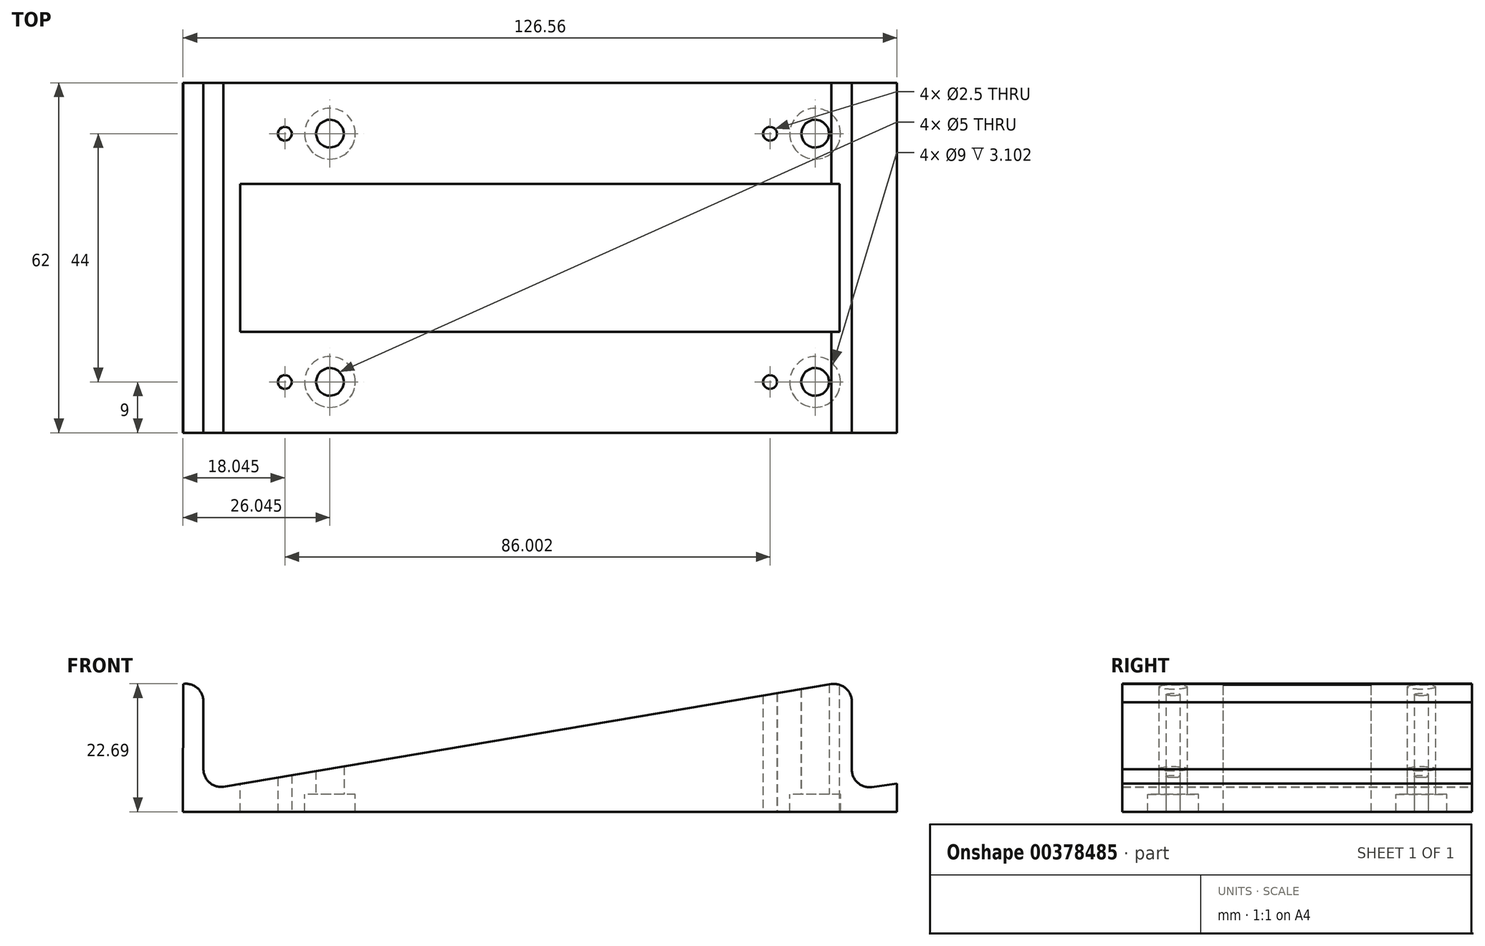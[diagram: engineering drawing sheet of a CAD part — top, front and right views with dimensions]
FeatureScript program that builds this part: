
annotation { "Feature Type Name" : "Feature", "Feature Type Description" : "" }
export const myFeature = defineFeature(function(context is Context, id is Id, definition is map)
    precondition{}
    {
        {
            var Q0;
            Q0=qCreatedBy(makeId("Front.planeOp"),FACE);
            var sketch = newSketch(context, id + "F0", { "sketchPlane" : qUnion([Q0])});
            skLineSegment(sketch, "E0", {"start": v(-59.65, 8.39) * mm, "end": v(-59.65, -3.51) * mm});
            skLineSegment(sketch, "E1", {"start": v(-56.14, -6.69) * mm, "end": v(51.65, 11.51) * mm});
            skLineSegment(sketch, "E2", {"start": v(58.81, -6.74) * mm, "end": v(63.28, -6.13) * mm});
            skLineSegment(sketch, "E3", {"start": v(63.28, -6.13) * mm, "end": v(63.28, -11.1) * mm});
            skLineSegment(sketch, "E4", {"start": v(63.28, -11.1) * mm, "end": v(-63.28, -11.1) * mm});
            skPoint(sketch, "E5.second.point", {"position": v(-62.39, -0.66) * mm});
            skPoint(sketch, "E5.third.point", {"position": v(-61.5, -0.4) * mm});
            skLineSegment(sketch, "E6", {"start": v(-63.28, -11.1) * mm, "end": v(-63.25, 11.55) * mm});
            skArc(sketch, "E7.trimOffspring", {"start": v(-59.65, 8.39) * mm, "mid": v(-60.72, 10.8) * mm, "end": v(-63.25, 11.55) * mm});
            skArc(sketch, "E8.trimOffspring", {"start": v(-59.65, -3.51) * mm, "mid": v(-58.62, -5.9) * mm, "end": v(-56.14, -6.69) * mm});
            skLineSegment(sketch, "E9", {"start": v(55.26, 8.33) * mm, "end": v(55.26, -3.56) * mm});
            skPoint(sketch, "E10.second.point", {"position": v(52.53, 5.28) * mm});
            skPoint(sketch, "E10.third.point", {"position": v(53.41, 5.54) * mm});
            skArc(sketch, "E11.trimOffspring", {"start": v(55.26, 8.33) * mm, "mid": v(54.2, 10.77) * mm, "end": v(51.65, 11.51) * mm});
            skArc(sketch, "E12.trimOffspring", {"start": v(55.26, -3.56) * mm, "mid": v(56.3, -5.97) * mm, "end": v(58.81, -6.74) * mm});
            skLineSegment(sketch, "E13", {"start": v(-63.25, 11.55) * mm, "end": v(74.42, 11.55) * mm, "construction": true});
            skSolve(sketch);
        }
        {
            var Q0;
            Q0=qSketchRegion(id+"F0",true);
            extrude(context, id + "F1", {"entities" : qUnion([Q0]), "depth" : 31 * mm});
        }
        {
            var Q0;
            Q0=makeQuery(id+"F1.opExtrude","SWEPT_BODY",BODY,{"disambiguationData":[OSD([sQuery(id+"F0.wireOp",EDGE,"X6rjagLQ-a7nE-w6Vv-3kkp-7P13FhxgeZci"),sQuery(id+"F0.wireOp",EDGE,"rJyHTlbv-r2ii-XpOz-qJYI-U7K787FcXT9B"),sQuery(id+"F0.wireOp",EDGE,"UvdABgA3-ZW4Q-jLAG-XZ58-KKb7sOvCEOLd"),sQuery(id+"F0.wireOp",EDGE,"8edDvAp8-Iqhi-MEnT-EPyK-PEICCKXdPERf"),sQuery(id+"F0.wireOp",EDGE,"5RGPJcfQ-oj1C-nyjU-RGCH-90OYZvmU7okd"),sQuery(id+"F0.wireOp",EDGE,"nuv1YldQ-uPeo-ucQy-kADE-yY51GJk1A8SW"),sQuery(id+"F0.wireOp",EDGE,"9IDJZypg-6hYg-XQDT-bXzg-yLjlFXgnIsPx"),sQuery(id+"F0.wireOp",EDGE,"5iBKq289-l9G4-ML6G-8Zm8-TBxTwmMSXo4c"),sQuery(id+"F0.wireOp",EDGE,"IRYstpvA-wG3c-Vhfm-dOiz-6G3TYm6s6ACp"),sQuery(id+"F0.wireOp",EDGE,"2tByvbzq-CgVc-BYaI-5mh9-BZhoFNA3rnU8"),sQuery(id+"F0.wireOp",EDGE,"J7kD6OiI-x1CE-zV7k-Ksf5-dgG7n0Ed7Lc8"),sQuery(id+"F0.wireOp",EDGE,"usFKVQ05-AxXf-UbQ5-ZF47-bucorxKLPDnf"),sQuery(id+"F0.wireOp",EDGE,"8tTMBYnK-jyrt-QZZi-OOM1-Ks7T1jKqHP4p"),sQuery(id+"F0.wireOp",EDGE,"aNOa8qk4-dDGC-TJfr-UsXt-0Z27L2bBaoPW"),sQuery(id+"F0.wireOp",EDGE,"co3yBv09-4AA5-sSzz-sbZm-wbczN9zzpFlO"),sQuery(id+"F0.wireOp",EDGE,"9luTmkGo-JmTk-WoZm-WdZi-2eskqThg4CA5"),sQuery(id+"F0.wireOp",EDGE,"QNMAagQt-4OmV-3ZdT-NZHn-lJ6LHsVNZ12A"),sQuery(id+"F0.wireOp",EDGE,"E0"),sQuery(id+"F0.wireOp",EDGE,"LaCQxE5r-Ou8T-tspR-dPCc-d2gM8dt26IJ4"),sQuery(id+"F0.wireOp",EDGE,"tysDmkrt-YQUX-nmhd-IIcf-EuzOKTVKjwW1"),sQuery(id+"F0.wireOp",EDGE,"8zM2XU66-CfLp-DSu5-ggFv-Xjqba4kKd3lN"),sQuery(id+"F0.wireOp",EDGE,"bxPwawIe-VsdV-0K0X-kh71-O9GE0I0d2Hzn"),sQuery(id+"F0.wireOp",EDGE,"Ta76Hruu-mcOr-gASH-Amss-OitY1s99El2f"),sQuery(id+"F0.wireOp",EDGE,"9uWYvEGJ-saeM-Nbb3-zuV6-ds3pb9swBQfK"),sQuery(id+"F0.wireOp",EDGE,"9eZR5atI-s3yS-Bz70-sCyy-oXYN0rDXefjr"),sQuery(id+"F0.wireOp",EDGE,"foBjDoMU-IZlR-ykUg-u7Yn-BJamdywYEiWy"),sQuery(id+"F0.wireOp",EDGE,"fnvSqjr0-rV7v-3WBg-xxCd-QbMLTEKwFvC4"),sQuery(id+"F0.wireOp",EDGE,"z3XylwKl-Yxo3-bV3A-yvAI-vIvSsyK3gtAu"),sQuery(id+"F0.wireOp",EDGE,"E1"),sQuery(id+"F0.wireOp",EDGE,"2c2nu2O0-qx7z-G40k-56CR-Hb7mX1kJGF1D"),sQuery(id+"F0.wireOp",EDGE,"W6u8q2Sr-tn2T-pBh1-jTxB-UCteOMF8OT5b"),sQuery(id+"F0.wireOp",EDGE,"SP8eBbsK-gR6C-g5yt-1Xhk-VaCtSweUHDhg"),sQuery(id+"F0.wireOp",EDGE,"F2eFEpuX-bTFf-0sAG-GLRY-GrkC39FuYopk"),sQuery(id+"F0.wireOp",EDGE,"B11oUoTT-6qet-d9Tf-xIA7-Onbt0dr6JRqB"),sQuery(id+"F0.wireOp",EDGE,"icmsBmHN-4xDo-8gjD-Ngl4-kt1qITF5Sr4D"),sQuery(id+"F0.wireOp",EDGE,"MzAjo3WH-x5B9-fS6W-S6Yf-auPV0ZSmn7rd"),sQuery(id+"F0.wireOp",EDGE,"3tkOM3FL-qgvZ-PLIy-XY6Q-vuf0hc8dh5GJ"),sQuery(id+"F0.wireOp",EDGE,"uJlCFYyk-phwo-ZUq8-5xq0-rSjuSznOMZrS"),sQuery(id+"F0.wireOp",EDGE,"mkuXqJka-q1Q0-TAYG-IULb-ylSPT2SN1lg7"),sQuery(id+"F0.wireOp",EDGE,"3tb4hQMN-rnYG-9bp3-TFDC-0CORyscKgtPi"),sQuery(id+"F0.wireOp",EDGE,"k8RofrE4-9yto-xs5X-iHqh-SwSJ6BzJapK2"),sQuery(id+"F0.wireOp",EDGE,"B3jP9m7T-Z5eZ-LDIi-yDtG-Dg3VGohJKm1n"),sQuery(id+"F0.wireOp",EDGE,"uTRBhaQw-5E8T-HzJf-HWhy-AwywLkO7PyXb"),sQuery(id+"F0.wireOp",EDGE,"8AnGxstQ-YUEf-PqRC-Jk94-XS2ZDdQA8w5O"),sQuery(id+"F0.wireOp",EDGE,"MfWv3BDd-mYij-3Hsb-bHTd-R6osLOgOeZMM"),sQuery(id+"F0.wireOp",EDGE,"10CaV5FA-CsxY-SnQw-EYj5-KfapEN4Iijd9"),sQuery(id+"F0.wireOp",EDGE,"ANFz48R1-M8Eg-dvWt-2c7c-Bwf9dMEtF9Db"),sQuery(id+"F0.wireOp",EDGE,"r5WBOgOA-zBjo-fWuJ-O3lp-0J2bBJtaSSIM"),sQuery(id+"F0.wireOp",EDGE,"AYO6whUn-QxFw-EXPK-BOOP-H87RD6U0aouA"),sQuery(id+"F0.wireOp",EDGE,"NcJYPMoa-uJqC-BgOU-yJQ6-4dZmMXDE3tKq"),sQuery(id+"F0.wireOp",EDGE,"M9dThICv-8CGM-sEGh-pd3K-8aR0dGVnCaAt"),sQuery(id+"F0.wireOp",EDGE,"E2"),sQuery(id+"F0.wireOp",EDGE,"E3"),sQuery(id+"F0.wireOp",EDGE,"E4"),sQuery(id+"F0.wireOp",EDGE,"GpYS4Pst-mkMX-w4Kb-Gbcn-fM3uJKyQqzig"),sQuery(id+"F0.wireOp",EDGE,"m2sXC5Oe-KpRQ-CKPd-uABx-7vzVF54k3vll")])]});
            var Q1;
            Q1=qCreatedBy(makeId("Front.planeOp"),FACE);
            mirror(context, id + "F2", {"operationType" : NewBodyOperationType.ADD, "entities" : qUnion([Q0]), "mirrorPlane" : qUnion([Q1])});
        }
        {
            var Q0;
            Q0=qCreatedBy(makeId("Top.planeOp"),FACE);
            var sketch = newSketch(context, id + "F3", { "sketchPlane" : qUnion([Q0])});
            skLineSegment(sketch, "E14.bottom", {"start": v(-53.1, -13.1) * mm, "end": v(53.11, -13.1) * mm});
            skLineSegment(sketch, "E14.top", {"start": v(-53.1, 0) * mm, "end": v(53.11, 0) * mm});
            skLineSegment(sketch, "E14.left", {"start": v(-53.1, -13.1) * mm, "end": v(-53.1, 0) * mm});
            skLineSegment(sketch, "E14.right", {"start": v(53.11, -13.1) * mm, "end": v(53.11, 0) * mm});
            skLineSegment(sketch, "E15.MirrorCS", {"start": v(-53.1, 13.1) * mm, "end": v(53.11, 13.1) * mm});
            skLineSegment(sketch, "E16.MirrorCS", {"start": v(-53.1, 13.1) * mm, "end": v(-53.1, 0) * mm});
            skLineSegment(sketch, "E17.MirrorCS", {"start": v(53.11, 13.1) * mm, "end": v(53.11, 0) * mm});
            skSolve(sketch);
        }
        {
            var Q0;
            Q0=qSketchRegion(id+"F3",true);
            extrude(context, id + "F4", {"entities" : qUnion([Q0]), "operationType" : NewBodyOperationType.REMOVE, "endBound" : BoundingType.SYMMETRIC, "oppositeDirection" : true, "depth" : 50 * mm});
        }
        {
            var Q0;
            Q0=qCreatedBy(makeId("Top.planeOp"),FACE);
            var sketch = newSketch(context, id + "F5", { "sketchPlane" : qUnion([Q0])});
            skCircle(sketch, "E18", {"center": v(-45.23, -22) * mm, "radius": 1.25 * mm});
            skPoint(sketch, "E18.first.point", {"position": v(-45.7, -20.84) * mm});
            skPoint(sketch, "E18.second.point", {"position": v(-44.77, -23.16) * mm});
            skPoint(sketch, "E18.third.point", {"position": v(-44.08, -21.53) * mm});
            skCircle(sketch, "E19", {"center": v(40.77, -22) * mm, "radius": 1.25 * mm});
            skPoint(sketch, "E19.first.point", {"position": v(40.3, -20.84) * mm});
            skPoint(sketch, "E19.second.point", {"position": v(41.23, -23.16) * mm});
            skPoint(sketch, "E19.third.point", {"position": v(41.92, -21.53) * mm});
            skCircle(sketch, "E20", {"center": v(-45.23, 22) * mm, "radius": 1.25 * mm});
            skCircle(sketch, "E21", {"center": v(40.77, 22) * mm, "radius": 1.25 * mm});
            skLineSegment(sketch, "E22", {"start": v(-45.23, 22) * mm, "end": v(-45.23, -22) * mm, "construction": true});
            skLineSegment(sketch, "E23", {"start": v(40.77, 22) * mm, "end": v(40.77, -22) * mm, "construction": true});
            skLineSegment(sketch, "E24", {"start": v(-45.23, -22) * mm, "end": v(-37.23, -22) * mm, "construction": true});
            skLineSegment(sketch, "E25", {"start": v(40.77, -22) * mm, "end": v(48.77, -22) * mm, "construction": true});
            skLineSegment(sketch, "E26", {"start": v(40.77, 22) * mm, "end": v(48.77, 22) * mm, "construction": true});
            skLineSegment(sketch, "E27", {"start": v(-45.23, 22) * mm, "end": v(-37.23, 22) * mm, "construction": true});
            skCircle(sketch, "E28", {"center": v(-37.23, 22) * mm, "radius": 2.5 * mm});
            skCircle(sketch, "E29", {"center": v(48.77, 22) * mm, "radius": 2.5 * mm});
            skCircle(sketch, "E30", {"center": v(48.77, -22) * mm, "radius": 2.5 * mm});
            skCircle(sketch, "E31", {"center": v(-37.23, -22) * mm, "radius": 2.5 * mm});
            skCircle(sketch, "E32", {"center": v(-37.23, 22) * mm, "radius": 4.5 * mm});
            skCircle(sketch, "E33", {"center": v(-37.23, -22) * mm, "radius": 4.5 * mm});
            skCircle(sketch, "E34", {"center": v(48.77, 22) * mm, "radius": 4.5 * mm});
            skCircle(sketch, "E35", {"center": v(48.77, -22) * mm, "radius": 4.5 * mm});
            skSolve(sketch);
        }
        {
            var Q0;
            Q0=makeQuery(id+"F5.imprint","IMPRINT",FACE,{"disambiguationData":[TD([[makeQuery(id+"F5.imprint","IMPRINT",EDGE,{"derivedFrom":sQuery(id+"F5.wireOp",EDGE,"E19")}),1.0]])]});
            var Q1;
            Q1=makeQuery(id+"F5.imprint","IMPRINT",FACE,{"disambiguationData":[TD([[makeQuery(id+"F5.imprint","IMPRINT",EDGE,{"derivedFrom":sQuery(id+"F5.wireOp",EDGE,"E18")}),1.0]])]});
            var Q2;
            Q2=makeQuery(id+"F5.imprint","IMPRINT",FACE,{"disambiguationData":[TD([[makeQuery(id+"F5.imprint","IMPRINT",EDGE,{"derivedFrom":sQuery(id+"F5.wireOp",EDGE,"E20")}),1.0]])]});
            var Q3;
            Q3=makeQuery(id+"F5.imprint","IMPRINT",FACE,{"disambiguationData":[TD([[makeQuery(id+"F5.imprint","IMPRINT",EDGE,{"derivedFrom":sQuery(id+"F5.wireOp",EDGE,"E21")}),1.0]])]});
            var Q4;
            Q4=makeQuery(id+"F5.imprint","IMPRINT",FACE,{"disambiguationData":[TD([[makeQuery(id+"F5.imprint","IMPRINT",EDGE,{"derivedFrom":sQuery(id+"F5.wireOp",EDGE,"E28")}),1.0]])]});
            var Q5;
            Q5=makeQuery(id+"F5.imprint","IMPRINT",FACE,{"disambiguationData":[TD([[makeQuery(id+"F5.imprint","IMPRINT",EDGE,{"derivedFrom":sQuery(id+"F5.wireOp",EDGE,"E31")}),1.0]])]});
            var Q6;
            Q6=makeQuery(id+"F5.imprint","IMPRINT",FACE,{"disambiguationData":[TD([[makeQuery(id+"F5.imprint","IMPRINT",EDGE,{"derivedFrom":sQuery(id+"F5.wireOp",EDGE,"E30")}),1.0]])]});
            var Q7;
            Q7=makeQuery(id+"F5.imprint","IMPRINT",FACE,{"disambiguationData":[TD([[makeQuery(id+"F5.imprint","IMPRINT",EDGE,{"derivedFrom":sQuery(id+"F5.wireOp",EDGE,"E29")}),1.0]])]});
            extrude(context, id + "F6", {"entities" : qUnion([Q0, Q1, Q2, Q3, Q4, Q5, Q6, Q7]), "operationType" : NewBodyOperationType.REMOVE, "endBound" : BoundingType.SYMMETRIC, "depth" : 30 * mm});
        }
        {
            var Q0;
            Q0=makeQuery(id+"F5.imprint","IMPRINT",FACE,{"disambiguationData":[TD([[makeQuery(id+"F5.imprint","IMPRINT",EDGE,{"derivedFrom":sQuery(id+"F5.wireOp",EDGE,"E28")}),-1.0]])]});
            var Q1;
            Q1=makeQuery(id+"F5.imprint","IMPRINT",FACE,{"disambiguationData":[TD([[makeQuery(id+"F5.imprint","IMPRINT",EDGE,{"derivedFrom":sQuery(id+"F5.wireOp",EDGE,"E31")}),-1.0]])]});
            var Q2;
            Q2=makeQuery(id+"F5.imprint","IMPRINT",FACE,{"disambiguationData":[TD([[makeQuery(id+"F5.imprint","IMPRINT",EDGE,{"derivedFrom":sQuery(id+"F5.wireOp",EDGE,"E29")}),-1.0]])]});
            var Q3;
            Q3=makeQuery(id+"F5.imprint","IMPRINT",FACE,{"disambiguationData":[TD([[makeQuery(id+"F5.imprint","IMPRINT",EDGE,{"derivedFrom":sQuery(id+"F5.wireOp",EDGE,"E30")}),-1.0]])]});
            extrude(context, id + "F7", {"entities" : qUnion([Q0, Q1, Q2, Q3]), "operationType" : NewBodyOperationType.REMOVE, "oppositeDirection" : true, "depth" : 12 * mm, "hasSecondDirection" : true, "secondDirectionOppositeDirection" : true, "secondDirectionDepth" : 8 * mm});
        }
    });
